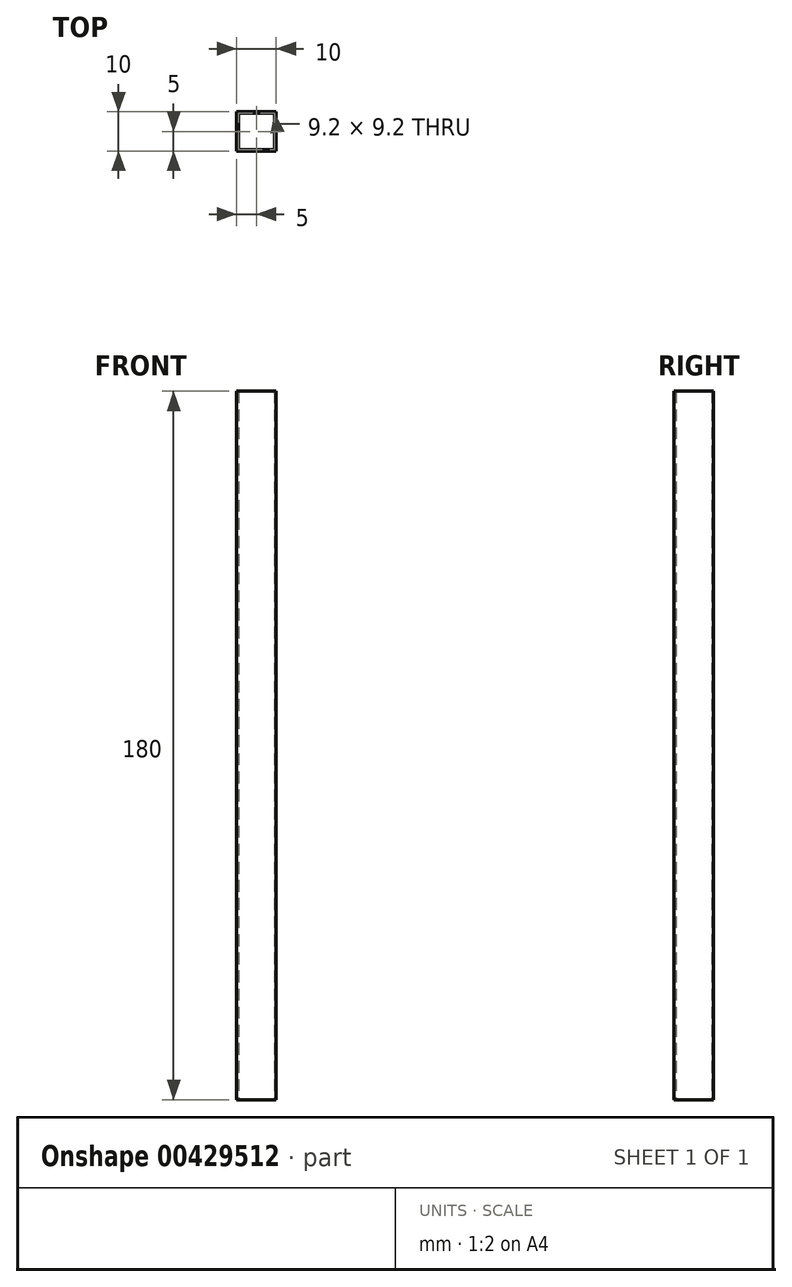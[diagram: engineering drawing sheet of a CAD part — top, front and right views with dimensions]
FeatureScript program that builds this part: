
annotation { "Feature Type Name" : "Feature", "Feature Type Description" : "" }
export const myFeature = defineFeature(function(context is Context, id is Id, definition is map)
    precondition{}
    {
        {
            var Q0;
            Q0=qCreatedBy(makeId("Top.planeOp"),FACE);
            var sketch = newSketch(context, id + "F0", { "sketchPlane" : qUnion([Q0])});
            skLineSegment(sketch, "E0.bottom", {"start": v(5, -5) * mm, "end": v(-5, -5) * mm});
            skLineSegment(sketch, "E0.top", {"start": v(5, 5) * mm, "end": v(-5, 5) * mm});
            skLineSegment(sketch, "E0.left", {"start": v(5, -5) * mm, "end": v(5, 5) * mm});
            skLineSegment(sketch, "E0.right", {"start": v(-5, -5) * mm, "end": v(-5, 5) * mm});
            skPoint(sketch, "E0.middle", {"position": v(0, 0) * mm});
            skLineSegment(sketch, "E1.0", {"start": v(4.6, 4.6) * mm, "end": v(-4.6, 4.6) * mm});
            skLineSegment(sketch, "E1.1", {"start": v(4.6, -4.6) * mm, "end": v(4.6, 4.6) * mm});
            skLineSegment(sketch, "E1.2", {"start": v(4.6, -4.6) * mm, "end": v(-4.6, -4.6) * mm});
            skLineSegment(sketch, "E1.3", {"start": v(-4.6, -4.6) * mm, "end": v(-4.6, 4.6) * mm});
            skSolve(sketch);
        }
        {
            var Q0;
            Q0=makeQuery(id+"F0.imprint","IMPRINT",FACE,{"disambiguationData":[TD([[makeQuery(id+"F0.imprint","IMPRINT",EDGE,{"derivedFrom":sQuery(id+"F0.wireOp",EDGE,"E0.bottom")}),-1.0]])]});
            var Q1;
            Q1=sQuery(id+"F0.wireOp",EDGE,"E1.1");
            var Q2;
            Q2=sQuery(id+"F0.wireOp",EDGE,"E0.left");
            var Q3;
            Q3=sQuery(id+"F0.wireOp",EDGE,"E0.top");
            var Q4;
            Q4=sQuery(id+"F0.wireOp",EDGE,"E1.0");
            var Q5;
            Q5=sQuery(id+"F0.wireOp",EDGE,"E0.right");
            var Q6;
            Q6=sQuery(id+"F0.wireOp",EDGE,"E1.3");
            var Q7;
            Q7=sQuery(id+"F0.wireOp",EDGE,"E1.2");
            var Q8;
            Q8=sQuery(id+"F0.wireOp",EDGE,"E0.bottom");
            extrude(context, id + "F1", {"entities" : qUnion([Q0]), "surfaceEntities" : qUnion([Q1, Q2, Q3, Q4, Q5, Q6, Q7, Q8]), "depth" : 180 * mm});
        }
    });
